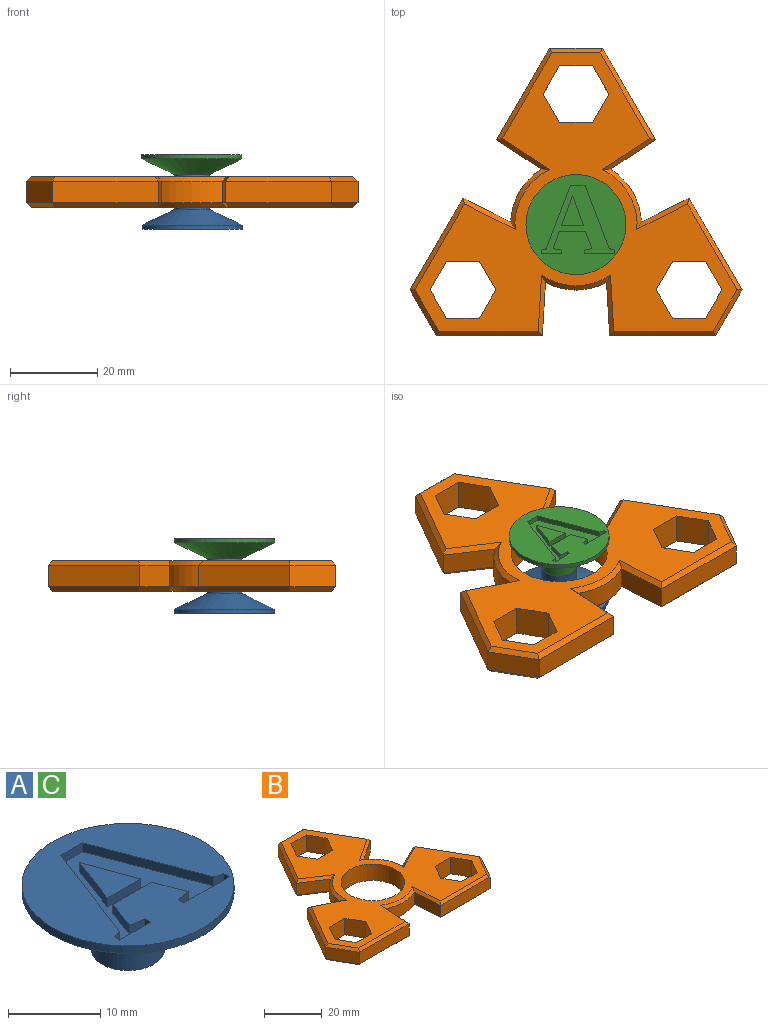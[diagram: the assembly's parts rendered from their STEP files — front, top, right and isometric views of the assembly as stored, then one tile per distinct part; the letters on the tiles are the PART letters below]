
ASSEMBLY  parts=3 mates=2
PART A: 26 faces, bbox 23x23x8.6 mm
  f0: plane 23x23mm, normal (0,0,1), area 302.9mm2, adj f2,f5,f6,f7,f8,f9,f10,f11
  f1: plane 7.95x7.95mm, normal (0,0,-1), area 49.6mm2, adj f4
  f2: cylinder r=11.5mm len=23mm, axis (0,0,-1), area 72.3mm2, adj f0,f3
  f3: cone r=3.98mm half-angle=64.4deg, axis (0,0,1), area 405.5mm2, adj f2,f4
  f4: cylinder r=3.98mm len=7.95mm, axis (0,0,-1), area 99.9mm2, adj f1,f3
  f5: plane 2.01x1.2mm, normal (-0.16,-0.99,0), area 2.4mm2, adj f0,f6,f23,f24
  f6: plane 4.04x1.43mm, normal (-0.94,0.33,0), area 5.1mm2, adj f0,f5,f7,f24
  f7: plane 6x1.2mm, normal (0,1,0), area 7.2mm2, adj f0,f6,f8,f24
  f8: plane 4.04x1.49mm, normal (0.94,0.35,0), area 5.2mm2, adj f0,f7,f9,f24
  f9: plane 1.81x1.2mm, normal (0.17,-0.98,0), area 2.2mm2, adj f0,f8,f10,f24
  f10: plane 1.2x0.85mm, normal (1,0,0), area 1mm2, adj f0,f9,f11,f24
  f11: plane 6.96x1.2mm, normal (0,1,0), area 8.3mm2, adj f0,f10,f12,f24
  f12: plane 1.2x0.85mm, normal (-1,0,0), area 1mm2, adj f0,f11,f13,f24
  f13: plane 1.2x1.19mm, normal (-0.26,-0.97,0), area 1.5mm2, adj f0,f12,f14,f24
  f14: plane 14.58x5.53mm, normal (-0.93,-0.35,0), area 18.7mm2, adj f0,f13,f15,f24
  f15: plane 3.38x1.2mm, normal (0,-1,0), area 4.1mm2, adj f0,f14,f16,f24
  f16: plane 14.58x5.56mm, normal (0.93,-0.36,0), area 18.7mm2, adj f0,f15,f17,f24
  f17: plane 1.2x1.16mm, normal (0.26,-0.96,0), area 1.4mm2, adj f0,f16,f18,f24
  f18: plane 1.2x0.85mm, normal (1,0,0), area 1mm2, adj f0,f17,f19,f24
  f19: plane 4.75x1.2mm, normal (0,1,0), area 5.7mm2, adj f0,f18,f23,f24
  f20: plane 6.91x2.5mm, normal (0.94,0.34,0), area 8.8mm2, adj f21,f22,f24,f25
  f21: plane 5.08x1.2mm, normal (0,-1,0), area 6.1mm2, adj f20,f22,f24,f25
  f22: plane 6.91x2.57mm, normal (-0.94,0.35,0), area 8.8mm2, adj f20,f21,f24,f25
  f23: plane 1.2x0.85mm, normal (-1,0,0), area 1mm2, adj f0,f5,f19,f24
  f24: plane 16.82x15.75mm, normal (0,0,1), area 95.1mm2, adj f5,f6,f7,f8,f9,f10,f11,f12
  f25: plane 6.91x5.08mm, normal (0,0,1), area 17.5mm2, adj f20,f21,f22
PART B: 75 faces, bbox 76.3x66.1x7 mm
  f0: cylinder r=15.04mm len=14.05mm, axis (0,0,-1), area 73.1mm2, adj f2,f6,f53,f59
  f1: cylinder r=15.04mm len=12.17mm, axis (0,0,-1), area 73.1mm2, adj f3,f5,f17,f52
  f2: cone r=15.04mm half-angle=45deg, axis (0,0,1), area 22.2mm2, adj f0,f21,f51,f67
  f3: cone r=15.04mm half-angle=45deg, axis (0,0,1), area 22.2mm2, adj f1,f21,f27,f50
  f4: cone r=14.04mm half-angle=45deg, axis (0,0,-1), area 22.2mm2, adj f12,f20,f32,f73
  f5: cone r=14.04mm half-angle=45deg, axis (0,0,-1), area 22.2mm2, adj f1,f20,f31,f49
  f6: cone r=14.04mm half-angle=45deg, axis (0,0,-1), area 22.2mm2, adj f0,f20,f48,f74
  f7: plane 7x6.54mm, normal (-0.87,0.5,0), area 52.8mm2, adj f8,f19,f20,f21
  f8: plane 7.55x7mm, normal (0,1,0), area 52.8mm2, adj f7,f9,f20,f21
  f9: plane 7x6.54mm, normal (0.87,0.5,0), area 52.8mm2, adj f8,f10,f20,f21
  f10: plane 7x6.54mm, normal (0.87,-0.5,0), area 52.8mm2, adj f9,f11,f20,f21
  f11: plane 7.55x7mm, normal (0,-1,0), area 52.8mm2, adj f10,f19,f20,f21
  f12: cylinder r=15.04mm len=12.17mm, axis (0,0,-1), area 73.1mm2, adj f4,f13,f26,f63
  f13: plane 10.25x6.74mm, normal (0.55,-0.84,0), area 61.3mm2, adj f12,f14,f24,f32
  f14: plane 21.07x12.16mm, normal (0.87,0.5,0), area 121.6mm2, adj f13,f15,f22,f30
  f15: plane 12.16x5mm, normal (0,1,0), area 60.8mm2, adj f14,f16,f23,f28
  f16: plane 21.07x12.16mm, normal (-0.87,0.5,0), area 121.6mm2, adj f15,f17,f25,f29
  f17: plane 10.25x6.74mm, normal (-0.55,-0.84,0), area 61.3mm2, adj f1,f16,f27,f31
  f18: cylinder r=11.04mm len=22.07mm, axis (0,0,-1), area 485.3mm2, adj f20,f21
  f19: plane 7x6.54mm, normal (-0.87,-0.5,0), area 52.8mm2, adj f7,f11,f20,f21
  f20: plane 73.98x64.07mm, normal (0,0,1), area 1578.1mm2, adj f4,f5,f6,f7,f8,f9,f10,f11
  f21: plane 73.98x64.07mm, normal (0,0,-1), area 1578.1mm2, adj f2,f3,f7,f8,f9,f10,f11,f18
  f22: plane 21.07x12.74mm, normal (0.61,0.35,-0.71), area 33.3mm2, adj f14,f21,f23,f24
  f23: plane 12.16x1mm, normal (0,0.71,-0.71), area 16.4mm2, adj f15,f21,f22,f25
  f24: plane 12.18x7.13mm, normal (0.39,-0.59,-0.71), area 17.8mm2, adj f13,f21,f22,f26
  f25: plane 21.07x12.74mm, normal (-0.61,0.35,-0.71), area 33.3mm2, adj f16,f21,f23,f27
  f26: cone r=15.04mm half-angle=45deg, axis (0,0,1), area 22.2mm2, adj f12,f21,f24,f69
  f27: plane 12.18x7.13mm, normal (-0.39,-0.59,-0.71), area 17.8mm2, adj f3,f17,f21,f25
  f28: plane 12.16x1mm, normal (0,0.71,0.71), area 16.4mm2, adj f15,f20,f29,f30
  f29: plane 21.07x12.74mm, normal (-0.61,0.35,0.71), area 33.3mm2, adj f16,f20,f28,f31
  f30: plane 21.07x12.74mm, normal (0.61,0.35,0.71), area 33.3mm2, adj f14,f20,f28,f32
  f31: plane 12.18x7.13mm, normal (-0.39,-0.59,0.71), area 17.8mm2, adj f5,f17,f20,f29
  f32: plane 12.18x7.13mm, normal (0.39,-0.59,0.71), area 17.8mm2, adj f4,f13,f20,f30
  f33: plane 10.54x6.08mm, normal (-0.87,-0.5,0), area 60.8mm2, adj f34,f35,f37,f46
  f34: plane 24.33x5mm, normal (0,-1,0), area 121.6mm2, adj f33,f38,f45,f53
  f35: plane 21.07x12.16mm, normal (-0.87,0.5,0), area 121.6mm2, adj f33,f36,f47,f52
  f36: plane 21.07x12.56mm, normal (-0.61,0.35,-0.71), area 33.3mm2, adj f21,f35,f37,f50
  f37: plane 10.54x6.66mm, normal (-0.61,-0.35,-0.71), area 16.4mm2, adj f21,f33,f36,f38
  f38: plane 24.33x1mm, normal (0,-0.71,-0.71), area 33.3mm2, adj f21,f34,f37,f51
  f39: plane 7x6.54mm, normal (0.87,-0.5,0), area 52.8mm2, adj f20,f21,f40,f44
  f40: plane 7x6.54mm, normal (0.87,0.5,0), area 52.8mm2, adj f20,f21,f39,f41
  f41: plane 7.55x7mm, normal (0,1,0), area 52.8mm2, adj f20,f21,f40,f42
  f42: plane 7x6.54mm, normal (-0.87,0.5,0), area 52.8mm2, adj f20,f21,f41,f43
  f43: plane 7x6.54mm, normal (-0.87,-0.5,0), area 52.8mm2, adj f20,f21,f42,f44
  f44: plane 7.55x7mm, normal (0,-1,0), area 52.8mm2, adj f20,f21,f39,f43
  f45: plane 24.33x1mm, normal (0,-0.71,0.71), area 33.3mm2, adj f20,f34,f46,f48
  f46: plane 10.54x6.66mm, normal (-0.61,-0.35,0.71), area 16.4mm2, adj f20,f33,f45,f47
  f47: plane 21.07x12.56mm, normal (-0.61,0.35,0.71), area 33.3mm2, adj f20,f35,f46,f49
  f48: plane 13.95x1.65mm, normal (0.71,-0.04,0.71), area 17.8mm2, adj f6,f20,f45,f53
  f49: plane 11.99x7.14mm, normal (0.32,0.63,0.71), area 17.8mm2, adj f5,f20,f47,f52
  f50: plane 11.99x7.14mm, normal (0.32,0.63,-0.71), area 17.8mm2, adj f3,f21,f36,f52
  f51: plane 13.95x1.65mm, normal (0.71,-0.04,-0.71), area 17.8mm2, adj f2,f21,f38,f53
  f52: plane 10.96x5.51mm, normal (0.45,0.89,0), area 61.3mm2, adj f1,f35,f49,f50
  f53: plane 12.24x5mm, normal (1,-0.06,0), area 61.3mm2, adj f0,f34,f48,f51
  f54: plane 7x6.54mm, normal (0.87,0.5,0), area 52.8mm2, adj f20,f21,f55,f64
  f55: plane 7x6.54mm, normal (0.87,-0.5,0), area 52.8mm2, adj f20,f21,f54,f56
  f56: plane 7.55x7mm, normal (0,-1,0), area 52.8mm2, adj f20,f21,f55,f57
  f57: plane 7x6.54mm, normal (-0.87,-0.5,0), area 52.8mm2, adj f20,f21,f56,f58
  f58: plane 7x6.54mm, normal (-0.87,0.5,0), area 52.8mm2, adj f20,f21,f57,f64
  f59: plane 12.24x5mm, normal (-1,-0.06,0), area 61.3mm2, adj f0,f60,f67,f74
  f60: plane 24.33x5mm, normal (0,-1,0), area 121.6mm2, adj f59,f61,f65,f72
  f61: plane 10.54x6.08mm, normal (0.87,-0.5,0), area 60.8mm2, adj f60,f62,f66,f70
  f62: plane 21.07x12.16mm, normal (0.87,0.5,0), area 121.6mm2, adj f61,f63,f68,f71
  f63: plane 10.96x5.51mm, normal (-0.45,0.89,0), area 61.3mm2, adj f12,f62,f69,f73
  f64: plane 7.55x7mm, normal (0,1,0), area 52.8mm2, adj f20,f21,f54,f58
  f65: plane 24.33x1mm, normal (0,-0.71,-0.71), area 33.3mm2, adj f21,f60,f66,f67
  f66: plane 10.54x6.66mm, normal (0.61,-0.35,-0.71), area 16.4mm2, adj f21,f61,f65,f68
  f67: plane 13.95x1.65mm, normal (-0.71,-0.04,-0.71), area 17.8mm2, adj f2,f21,f59,f65
  f68: plane 21.07x12.56mm, normal (0.61,0.35,-0.71), area 33.3mm2, adj f21,f62,f66,f69
  f69: plane 11.99x7.14mm, normal (-0.32,0.63,-0.71), area 17.8mm2, adj f21,f26,f63,f68
  f70: plane 10.54x6.66mm, normal (0.61,-0.35,0.71), area 16.4mm2, adj f20,f61,f71,f72
  f71: plane 21.07x12.56mm, normal (0.61,0.35,0.71), area 33.3mm2, adj f20,f62,f70,f73
  f72: plane 24.33x1mm, normal (0,-0.71,0.71), area 33.3mm2, adj f20,f60,f70,f74
  f73: plane 11.99x7.14mm, normal (-0.32,0.63,0.71), area 17.8mm2, adj f4,f20,f63,f71
  f74: plane 13.95x1.65mm, normal (-0.71,-0.04,0.71), area 17.8mm2, adj f6,f20,f59,f72
PART C: same geometry as A
PLACE A rot(axis=(0,1,0),180deg) t=(8.49,0.47,26.69)mm
PLACE B t=(8.49,0.47,23.19)mm
PLACE C t=(8.49,0.47,26.69)mm
MATE revolute A.f2 <-> B.f18  axis (0,0,1) through (8.49,0.47,22.69)mm
MATE revolute B.f18 <-> C.f2  axis (0,0,1) through (8.49,0.47,30.19)mm
